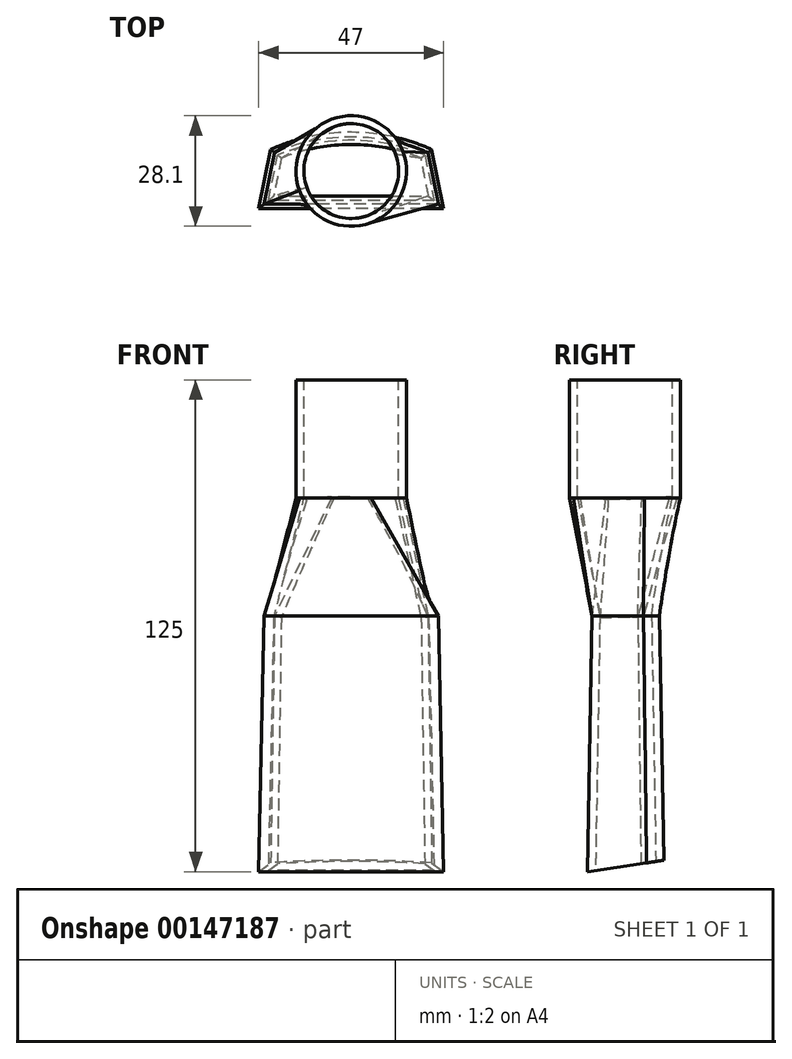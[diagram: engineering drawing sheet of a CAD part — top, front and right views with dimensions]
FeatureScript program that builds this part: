
annotation { "Feature Type Name" : "Feature", "Feature Type Description" : "" }
export const myFeature = defineFeature(function(context is Context, id is Id, definition is map)
    precondition{}
    {
        {
            var Q0;
            Q0=qCreatedBy(makeId("Top.planeOp"),FACE);
            var sketch = newSketch(context, id + "F12", { "sketchPlane" : qUnion([Q0])});
            skLineSegment(sketch, "E0", {"start": v(0, 0) * mm, "end": v(47, 0) * mm});
            skLineSegment(sketch, "E1", {"start": v(47, 0) * mm, "end": v(44, 15) * mm});
            skArc(sketch, "E2", {"start": v(44, 15) * mm, "mid": v(23.5, 19.4) * mm, "end": v(3, 15) * mm});
            skLineSegment(sketch, "E3", {"start": v(3, 15) * mm, "end": v(0, 0) * mm});
            skSolve(sketch);
        }
        {
            var Q0;
            Q0=makeQuery(id+"F12.imprint","IMPRINT",FACE,{"disambiguationData":[TD([[makeQuery(id+"F12.imprint","IMPRINT",EDGE,{"derivedFrom":sQuery(id+"F12.wireOp",EDGE,"E0")}),1.0]])]});
            extrude(context, id + "F0", {"entities" : qUnion([Q0]), "depth" : 65 * mm, "hasDraft" : true, "draftAngle" : 1 * degree, "draftPullDirection" : true});
        }
        {
            var Q0;
            Q0=qCreatedBy(makeId("Right.planeOp"),FACE);
            var sketch = newSketch(context, id + "F1", { "sketchPlane" : qUnion([Q0])});
            skLineSegment(sketch, "E4", {"start": v(0, 0) * mm, "end": v(25.97, 3.93) * mm});
            skLineSegment(sketch, "E5", {"start": v(25.97, 3.93) * mm, "end": v(25.97, 3.93) * mm});
            skLineSegment(sketch, "E6", {"start": v(25.97, 3.93) * mm, "end": v(27.55, -6.5) * mm});
            skLineSegment(sketch, "E7", {"start": v(27.55, -6.5) * mm, "end": v(27.46, -6.74) * mm});
            skLineSegment(sketch, "E8", {"start": v(27.46, -6.74) * mm, "end": v(-2.05, -6.74) * mm});
            skLineSegment(sketch, "E9", {"start": v(-2.05, -6.74) * mm, "end": v(0, 0) * mm});
            skSolve(sketch);
        }
        {
            var Q0;
            Q0=makeQuery(id+"F1.imprint","IMPRINT",FACE,{"disambiguationData":[TD([[makeQuery(id+"F1.imprint","IMPRINT",EDGE,{"derivedFrom":sQuery(id+"F1.wireOp",EDGE,"E4")}),-1.0]])]});
            extrude(context, id + "F2", {"entities" : qUnion([Q0]), "operationType" : NewBodyOperationType.REMOVE, "depth" : 100 * mm});
        }
        {
            var Q0;
            Q0=makeQuery(id+"F0.opExtrude","CAP_FACE",FACE,{"disambiguationData":[OSD([sQuery(id+"F12.wireOp",EDGE,"E0"),sQuery(id+"F12.wireOp",EDGE,"E1"),sQuery(id+"F12.wireOp",EDGE,"E2"),sQuery(id+"F12.wireOp",EDGE,"E3")])],"isStart":false});
            cPlane(context, id + "F3", {"entities" : qUnion([Q0]), "cplaneType" : CPlaneType.OFFSET, "offset" : 30 * mm, "width" : 150 * mm, "height" : 150 * mm});
        }
        {
            var Q0;
            Q0=qCreatedBy(id+"F3.planeOp",FACE);
            var sketch = newSketch(context, id + "F4", { "sketchPlane" : qUnion([Q0])});
            skCircle(sketch, "E10", {"center": v(23.5, 9.5) * mm, "radius": 14.05 * mm});
            skSolve(sketch);
        }
        {
            var Q1;
            Q1=makeQuery(id+"F4.imprint","IMPRINT",FACE,{"disambiguationData":[TD([[makeQuery(id+"F4.imprint","IMPRINT",EDGE,{"derivedFrom":sQuery(id+"F4.wireOp",EDGE,"E10")}),1.0]])]});
            var Q2;
            Q2=makeQuery(id+"F0.opExtrude","CAP_FACE",FACE,{"disambiguationData":[OSD([sQuery(id+"F12.wireOp",EDGE,"E0"),sQuery(id+"F12.wireOp",EDGE,"E1"),sQuery(id+"F12.wireOp",EDGE,"E2"),sQuery(id+"F12.wireOp",EDGE,"E3")])],"isStart":false});
            loft(context, id + "F5", {"operationType" : NewBodyOperationType.ADD, "sheetProfilesArray" : [{ "sheetProfileEntities" : qUnion([Q1]) }, { "sheetProfileEntities" : qUnion([Q2]) }]});
        }
        {
            var Q0;
            Q0=makeQuery(id+"F5.opLoft","CAP_FACE",FACE,{"disambiguationData":[OSD([makeQuery(id+"F4.imprint","IMPRINT",FACE,{"disambiguationData":[TD([[makeQuery(id+"F4.imprint","IMPRINT",EDGE,{"derivedFrom":sQuery(id+"F4.wireOp",EDGE,"E10")}),1.0]])]})])],"isStart":true});
            var sketch = newSketch(context, id + "F6", { "sketchPlane" : qUnion([Q0])});
            skCircle(sketch, "E11", {"center": v(23.5, 9.5) * mm, "radius": 14.05 * mm});
            skSolve(sketch);
        }
        {
            var Q0;
            {var subQ0=sQuery(id+"F6.wireOp",EDGE,"E11");var subQ1=makeQuery(id+"F6.imprint","IMPRINT",VERTEX,{"disambiguationData":[OD(1.0)],"derivedFrom":subQ0});Q0=makeQuery(id+"F6.imprint","IMPRINT",FACE,{"disambiguationData":[TD([[makeQuery(id+"F6.imprint","IMPRINT",EDGE,{"disambiguationData":[TD([[subQ1,1.0]])],"derivedFrom":subQ0}),1.0]])]});}
            extrude(context, id + "F7", {"entities" : qUnion([Q0]), "depth" : 30 * mm});
        }
        {
            var Q0;
            Q0=makeQuery(id+"F7.opExtrude","SWEPT_BODY",BODY,{"disambiguationData":[OSD([sQuery(id+"F6.wireOp",EDGE,"E11")])]});
            deleteBodies(context, id + "F8", {"entities" : qUnion([Q0])});
        }
        {
            var Q0;
            Q0=makeQuery(id+"F5.opLoft","CAP_FACE",FACE,{"disambiguationData":[OSD([makeQuery(id+"F4.imprint","IMPRINT",FACE,{"disambiguationData":[TD([[makeQuery(id+"F4.imprint","IMPRINT",EDGE,{"derivedFrom":sQuery(id+"F4.wireOp",EDGE,"E10")}),1.0]])]})])],"isStart":true});
            var sketch = newSketch(context, id + "F9", { "sketchPlane" : qUnion([Q0])});
            skCircle(sketch, "E12", {"center": v(23.5, 9.5) * mm, "radius": 14.05 * mm});
            skSolve(sketch);
        }
        {
            var Q0;
            Q0 = qSketchRegion(id + "F9", true);
            extrude(context, id + "F10", {"entities" : qUnion([Q0]), "operationType" : NewBodyOperationType.ADD, "depth" : 30 * mm});
        }
        {
            var Q0;
            Q0=makeQuery(id+"F10.opExtrude","CAP_FACE",FACE,{"disambiguationData":[OSD([sQuery(id+"F9.wireOp",EDGE,"E12")])],"isStart":false});
            var Q1;
            Q1=makeQuery(id+"F2.boolean.opBoolean","COPY",FACE,{"derivedFrom":makeQuery(id+"F2.opExtrude","SWEPT_FACE",FACE,{"disambiguationData":[OSD([sQuery(id+"F1.wireOp",EDGE,"E4")])]})});
            shell(context, id + "F11", {"entities" : qUnion([Q0, Q1]), "thickness" : 2 * mm});
        }
    });
